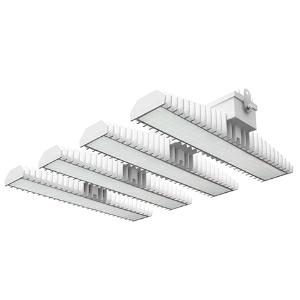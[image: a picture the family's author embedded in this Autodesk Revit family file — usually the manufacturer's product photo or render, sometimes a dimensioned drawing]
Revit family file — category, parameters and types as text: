
# Revit family: 3f_filippi_-_3f_lem_ampio_3f_filippi_-_58884_a0812_-_3f_lem_4_led_200_cr_ampio___vs_95bc
name_source: partatom
category: Lighting Fixtures
units: mm (PartAtom-declared; Revit-internal decimal feet)

## family parameters
Cut with Voids When Loaded = No
Host = Face
Light Source = No
Part Type = Normal
Room Calculation Point = No
Round Connector Dimension = Use Diameter
Shared = No

## types (1)
- 3F Filippi - 3F LEM Ampio (1 x LED, 26607 lm, 218 W, 4000 K)
    Apparent Load = 218 VA
    Approval mark = CE
    CIE Flux Codes = 67 90 97 100 100
    Color Rendering = 80
    Color Temperature = 4000 K
    Control Gear = Electronic ballast
    Default Elevation = 1800 mm
    Description = Industrial luminaire with high light output and high luminous efficiency designed with the most innovative technologies for environments with temperature up to 55°C.

ILLUMINOTECHNICAL
Luminous efficiency 100% (DLOR 98%, ULOR 2%).
Initial luminous flux of the luminaire 26607 lm.
Direct symmetric wide distribution: the illuminated area has a rectangular shape.
Installation Interdistance Transv.D = 1.24 x hu - Long.D = 1.20 x hu.
Tabular UGR (CIE 117 - 4H-8H; S=0.25H; 70/50/20): RUG 22.8 - 22.9.
Beam angle: 82° - 83°.
Luminous efficacy 122 lm/W.
Lifetime (L93/B10): 30000 h. (tq+25°C)
Lifetime (L90/B10): 50000 h. (tq+25°C)
Lifetime (L85/B10): 80000 h. (tq+25°C)
Lifetime (L80/B10): 100000 h. (tq+25°C)
Lifetime (L85/B10): 50000 h. (tq+55°C)
Sudden decreased luminous flux after 50000 hours: 0% (C0).
Photobiological safety in compliance with IEC/TR 62778: RG0 risk exempt, (IEC 62471).
In compliance with IEC/EN 62722-2-1 - IEC/EN 62717 standards.

SOURCE
4 Mid-Power linear LED modules 50W/840.
Energy efficiency class (UE 2019/2020 - UE 2019/2015): C.
CIE 13.3 Colour rendering index: CRI >80 (R9 <50%).
IES TM-30 Fidelity Index: Rf = 84 Rg = 95.
CCT nominal colour temperature 4000 K.
Colour initial tolerance (MacAdam): SDCM 3.

MECHANICAL
Passive modular heatsinks in die-casted aluminium, painted in white colour.
To optimize the thermal management of the LED module, the heatsinks are oversized and provided with self-cleaning of cooling fins.
Wiring body in aluminium and galvanised steel anchored solidly to the sinks and thermally separated.
3F Lens lenses with high luminous efficiency, transparent methacrylate (PMMA), fixed to the LED modules.
Fixing brackets in stainless steel.
Luminaire with limited surface temperature. - D - (EN 60598-2-24)
Dimensions: 757x542 mm, height 133 mm. Weight 19.305 kg.
IP65 protection degree.
Mechanical strength to impacts IK06 (1 joule).
Glow-wire test resistance 650°C.

ELECTRICAL
Halogen Free electronic wiring 230V-50/60Hz, power factor 0.97, THD <25%, constant output current, class I, 2 driver.
Power of the luminaire 218 W.
ENEC - CE.
SAFE FLICKER: PstLM=<1 and SVM=<0.4 (IEC TR 61547-1 and IEC TR 63158), to ensure a more comfortable and safe light.
Luminaire compliant with EN 60598-2-22 for power supply from a centralised emergency system CPSS (Central Power Supply System), not incorporated in the luminaire - high risk areas excluded. The default power and flux are 100% in AC and 100% in DC.
Ambient temperature from -30°C to +55°C.
Temperature class T6 max 85°C.
Quick connection via M20 3P connector with 9-13 mm tightening range.
Power unit positioned on a separate compartment by the LED module to ensure optimum temperatures of cabling components, to be inspectable and maintainable.
Relative humidity UR: <85%.

INSTALLATION
Ceiling / Suspended / Wall.
All accessories dedicated to this product are available on the Catalog and on our website www.3F-Filippi.com.

ACCESSORIES
A0812 - Anti-glare microprismatic VS moulded glass, tempered, not flammable, with sealing gasket.
One required for each light module. The pack contains 10 pieces.

APPLICATIONS
In commercial environments, exhibition and industrial areas, stores, open areas.
Applications with high ambient temperature up to 55°C.
Environments in which it is necessary a total protection against falling fragments (eg environments with foodstuffs or machines with moving parts or with extreme temperature changes), use luminaires with polycarbonate lenses.

WARNING
Fixture not suitable for cold stores with an ambient temperature <0°C and/or relative humidity >85%.
Luminaire designed for disposal/recycling at end-of-life.
Replaceable (LED only) light source by a professional. Replaceable control gear by a professional.
    Height = 133 mm
    Lamp = 1 x LED
    Lamp Light Flux = 26607 lm
    Lamp Power = 218 W
    Lamp count = 1
    Length = 757 mm
    Lifetime = 50000 h
    Luminous efficacy = 122 lm/W
    Manufacturer = 3F Filippi
    ModVariant = No
    Model = 3F Filippi - 58884+A0812 - 3F LEM 4 LED 200 CR AMPIO + VS
    Mounting Place = Ceiling
    Mounting Type = Pendant
    Number of Poles = 1
    OnlyDefault = Yes
    Power Factor = 1
    Product Name = 3F Filippi - 3F LEM Ampio
    Product group = pendant luminaire
    ProductGroupID = 9
    Protection Class = Protection class I
    Protection Degree = IP 65
    RLX_Detail_Level = 1
    RLX_Emergency_Light_Flux = 0 lm
    RLX_Emergency_Type = 0
    RLX_Emergency_Type_DB = No
    RlxData = <blob elided: 120189 chars, md5=9462cd64>
    Socket = socket
    Standby Power = 0 W
    System Light Flux = 26607 lm
    System Power = 218 W
    Type Comments = Product without accessories
    Type Image = 3f_filippi_-_lem_4__a0812.jpg
    URL = http://relux.com
    VarID = ---
    Voltage = 0 V
    Weight = 0.00 kg
    Width = 542 mm

## geometry (parser evidence)
native form markers: Blend x4, Sweep x12
no freeform markers — native parametric forms only
